# Revit family: СИБИТ_Плита_Перекрытия_Ширина 295 мм_ГОСТ 19570-74
name_source: partatom
category: Каркас несущий
revit_build: Autodesk Revit 2017 (Build: 20171027_0315(x64)
units: mm (PartAtom-declared; Revit-internal decimal feet)

## family parameters
Всегда вертикально = Нет
Всегда экспортировать в виде геометрии = Нет
Заголовок OmniClass = Concrete Structural Floor Decks
Материал для поведения модели = Сборный железобетон
На основе рабочей плоскости = Да
Номер OmniClass = 23.25.30.27.11.11
Общий = Нет
Округление длины несущего каркаса = 0 мм
Показывать семейство разрезанным на планах = Да
При загрузке вырезать с полостями = Нет
Скрытие кромок = Другими элементами
Условное обозначение = Из семейства
Форма сечения = Не задано

## types (1)
- СИБИТ_Плита_Перекрытия_Ширина 295 мм_ГОСТ 19570-74
    Bimon = www.bimon.ru
    IFC Classification = IfcSlab FLOOR
    Masterformat Code = 03 41 16
    Masterformat Title = Precast Concrete Slabs
    Omniclass Code = 23-13 17 15
    Omniclass Title = Precast Profiles
    UNSPSC Code = 30121704
    UNSPSC Title = Concrete slab
    URL = www.sibyt.ru
    Uniclass 2015 Code = Pr_20_85_14_16
    Uniclass 2015 Title = Concrete solid slabs
    Изготовитель = Завод "СИБИТ"
    Контактный телефон = +7 (383) 363-90-90
    Материал плиты = СИБИТ_Перекрытия_Газобетон D600 B3,5
    Описание = Панель перекрытий из автоклавного ячеистого бетона ГОСТ 19570-74
    Отметка по умолчанию = 1219 мм
    Разработчик модели = Bimon - сервисный провайдер услуг информационного моделирования
    Сертификат соответствия = https://sibyt.ru
    Таблица_выбора = SLT_Перекрытия_295
    Тип_1 = Длина : 1940 мм
    Тип_1.1 = Заполнение : Обвязочный пояс справа
    Тип_1.2 = Заполнение : Обвязочный пояс слева
    Тип_1.3 = Заполнение : Без заполнения
    Тип_1.4 = Заполнение : Заполнение шва между плитами
    Тип_10 = Длина : 3740 мм
    Тип_11 = Длина : 3940 мм
    Тип_12 = Длина : 4040 мм
    Тип_13 = Длина : 4140 мм
    Тип_14 = Длина : 4240 мм
    Тип_15 = Длина : 4440 мм
    Тип_16 = Длина : 4740 мм
    Тип_17 = Длина : 4940 мм
    Тип_18 = Длина : 5040 мм
    Тип_19 = Длина : 5240 мм
    Тип_2 = Длина : 2240 мм
    Тип_2.1 = Вид заполнения : Пояс обвязочный
    Тип_2.2 = Вид заполнения : Без заполнения
    Тип_2.3 = Вид заполнения : Шов между плитами
    Тип_20 = Длина : 5440 мм
    Тип_21 = Длина : 5740 мм
    Тип_22 = Длина : 5940 мм
    Тип_3 = Длина : 2440 мм
    Тип_4 = Длина : 2740 мм
    Тип_5 = Длина : 2940 мм
    Тип_6 = Длина : 3040 мм
    Тип_7 = Длина : 3140 мм
    Тип_8 = Длина : 3240 мм
    Тип_9 = Длина : 3440 мм

## geometry (parser evidence)
native form markers: Blend x5
no freeform markers — native parametric forms only
